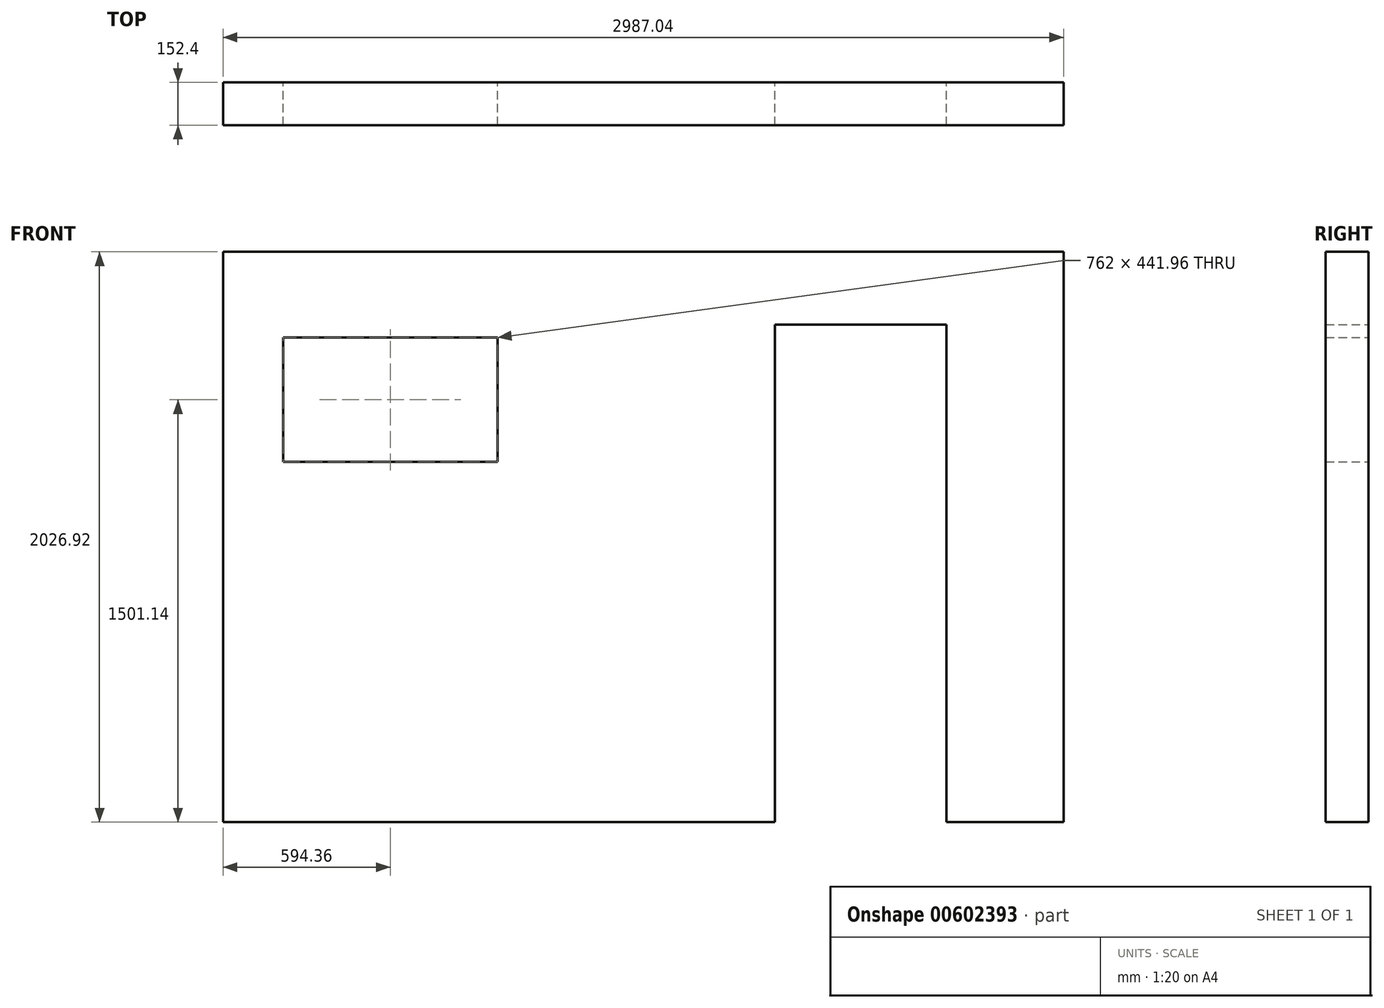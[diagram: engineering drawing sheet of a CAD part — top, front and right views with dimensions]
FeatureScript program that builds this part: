
annotation { "Feature Type Name" : "Feature", "Feature Type Description" : "" }
export const myFeature = defineFeature(function(context is Context, id is Id, definition is map)
    precondition{}
    {
        {
            var Q0;
            Q0=qCreatedBy(makeId("Front.planeOp"),FACE);
            var sketch = newSketch(context, id + "F0", { "sketchPlane" : qUnion([Q0])});
            skLineSegment(sketch, "E0.bottom", {"start": v(-1493.52, 1013.46) * mm, "end": v(1493.52, 1013.46) * mm});
            skLineSegment(sketch, "E0.top", {"start": v(-1493.52, -1013.46) * mm, "end": v(1493.52, -1013.46) * mm});
            skLineSegment(sketch, "E0.left", {"start": v(-1493.52, 1013.46) * mm, "end": v(-1493.52, -1013.46) * mm});
            skLineSegment(sketch, "E0.right", {"start": v(1493.52, 1013.46) * mm, "end": v(1493.52, -1013.46) * mm});
            skPoint(sketch, "E0.middle", {"position": v(0, 0) * mm});
            skLineSegment(sketch, "E1.bottom", {"start": v(1077.28, -1013.46) * mm, "end": v(467.68, -1013.46) * mm});
            skLineSegment(sketch, "E1.top", {"start": v(1077.28, 754.38) * mm, "end": v(467.68, 754.38) * mm});
            skLineSegment(sketch, "E1.left", {"start": v(1077.28, -1013.46) * mm, "end": v(1077.28, 754.38) * mm});
            skLineSegment(sketch, "E1.right", {"start": v(467.68, -1013.46) * mm, "end": v(467.68, 754.38) * mm});
            skLineSegment(sketch, "E2.bottom", {"start": v(-1280.16, 708.66) * mm, "end": v(-518.16, 708.66) * mm});
            skLineSegment(sketch, "E2.top", {"start": v(-1280.16, 266.7) * mm, "end": v(-518.16, 266.7) * mm});
            skLineSegment(sketch, "E2.left", {"start": v(-1280.16, 708.66) * mm, "end": v(-1280.16, 266.7) * mm});
            skLineSegment(sketch, "E2.right", {"start": v(-518.16, 708.66) * mm, "end": v(-518.16, 266.7) * mm});
            skPoint(sketch, "E2.middle", {"position": v(-899.16, 487.68) * mm});
            skSolve(sketch);
        }
        {
            var Q0;
            Q0=makeQuery(id+"F0.imprint","IMPRINT",FACE,{"disambiguationData":[TD([[makeQuery(id+"F0.imprint","IMPRINT",EDGE,{"derivedFrom":sQuery(id+"F0.wireOp",EDGE,"E0.bottom")}),-1.0]])]});
            extrude(context, id + "F1", {"entities" : qUnion([Q0]), "depth" : 152.4 * mm, "offsetDistance" : 30.48 * mm});
        }
    });
